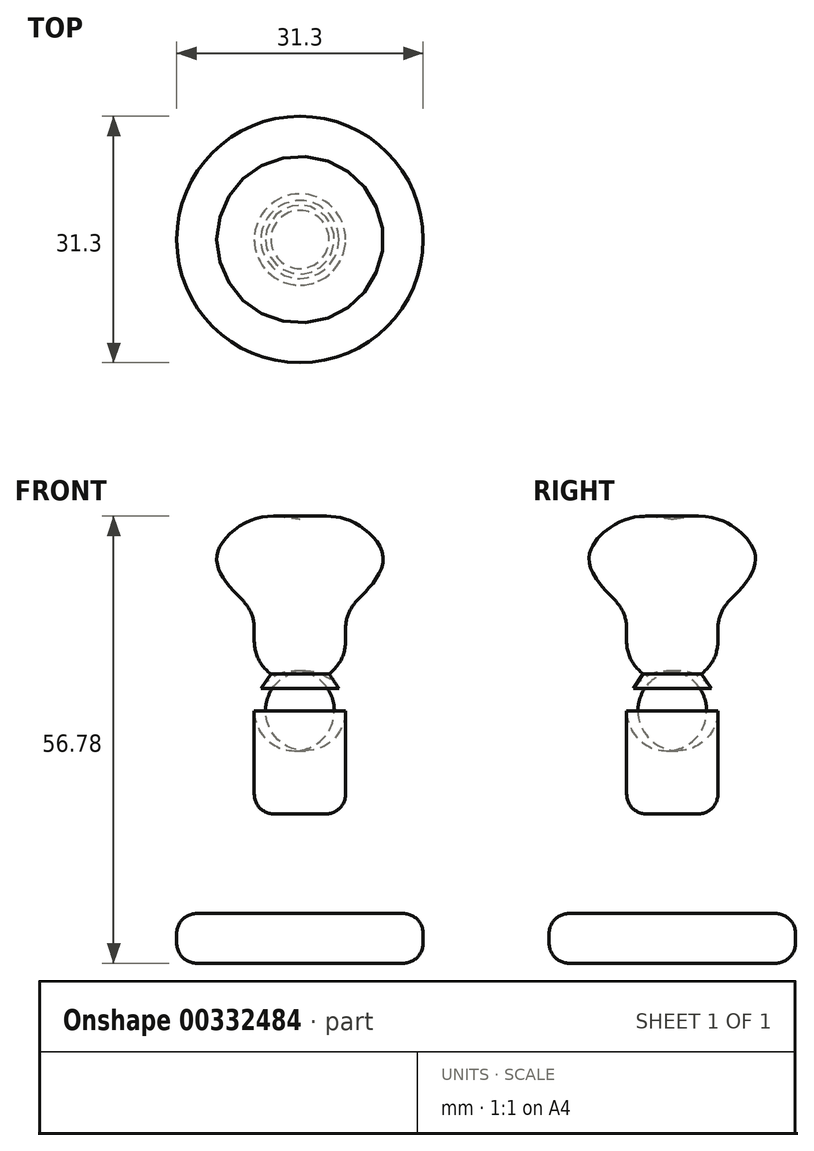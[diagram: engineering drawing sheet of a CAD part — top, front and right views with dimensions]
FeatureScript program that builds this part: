
annotation { "Feature Type Name" : "Feature", "Feature Type Description" : "" }
export const myFeature = defineFeature(function(context is Context, id is Id, definition is map)
    precondition{}
    {
        {
            var Q0;
            Q0=qCreatedBy(makeId("Front.planeOp"),FACE);
            var sketch = newSketch(context, id + "F0", { "sketchPlane" : qUnion([Q0])});
            skLineSegment(sketch, "E0.bottom", {"start": v(0, -56.42) * mm, "end": v(-15.65, -56.42) * mm});
            skLineSegment(sketch, "E0.top", {"start": v(0, -50.1) * mm, "end": v(-15.65, -50.1) * mm});
            skLineSegment(sketch, "E0.left", {"start": v(0, -56.42) * mm, "end": v(0, -50.1) * mm});
            skLineSegment(sketch, "E0.right", {"start": v(-15.65, -56.42) * mm, "end": v(-15.65, -50.1) * mm});
            skLineSegment(sketch, "E1.bottom", {"start": v(0, -50.1) * mm, "end": v(-14.3, -50.1) * mm});
            skLineSegment(sketch, "E1.top", {"start": v(0, -44.24) * mm, "end": v(-14.3, -44.24) * mm});
            skLineSegment(sketch, "E1.left", {"start": v(0, -50.1) * mm, "end": v(0, -44.24) * mm});
            skLineSegment(sketch, "E1.right", {"start": v(-14.3, -50.1) * mm, "end": v(-14.3, -44.24) * mm});
            skLineSegment(sketch, "E2.bottom", {"start": v(0, -44.24) * mm, "end": v(-11.6, -44.24) * mm});
            skLineSegment(sketch, "E2.top", {"start": v(0, -37.47) * mm, "end": v(-11.6, -37.47) * mm});
            skLineSegment(sketch, "E2.left", {"start": v(0, -44.24) * mm, "end": v(0, -37.47) * mm});
            skLineSegment(sketch, "E2.right", {"start": v(-11.6, -44.24) * mm, "end": v(-11.6, -37.47) * mm});
            skLineSegment(sketch, "E3", {"start": v(-5.8, -37.47) * mm, "end": v(-5.8, -22.81) * mm});
            skLineSegment(sketch, "E4", {"start": v(-5.8, -22.81) * mm, "end": v(-3.7, -19.65) * mm});
            skLineSegment(sketch, "E5", {"start": v(-3.7, -19.65) * mm, "end": v(-5.8, -18.26) * mm});
            skLineSegment(sketch, "E6", {"start": v(-5.8, -18.26) * mm, "end": v(-5.8, -11.76) * mm});
            skFitSpline(sketch, "E7", {"points": [v(-5.8, -11.76) * mm, v(-10.01, -7.02) * mm, v(-10.24, -3.64) * mm, v(-5.8, 0) * mm, v(0, 0) * mm], "startDerivative": vector(-18.47, 17.4) * mm, "endDerivative": vector(22.22, -3.54) * mm});
            skFitSpline(sketch, "E8", {"points": [v(-5.8, -11.76) * mm, v(0, -11.76) * mm], "startDerivative": vector(5.8, 0) * mm, "endDerivative": vector(5.8, 0) * mm});
            skLineSegment(sketch, "E9", {"start": v(0, 0) * mm, "end": v(0, -56.42) * mm});
            skSolve(sketch);
        }
        {
            var Q0;
            {var subQ1=sQuery(id+"F0.wireOp",EDGE,"E0.bottom");Q0=makeQuery(id+"F0.imprint","IMPRINT",FACE,{"disambiguationData":[TD([[makeQuery(id+"F0.imprint","IMPRINT",EDGE,{"derivedFrom":subQ1}),-1.0]])]});}
            var Q1;
            {var subQ1=sQuery(id+"F0.wireOp",EDGE,"E1.bottom");Q1=makeQuery(id+"F0.imprint","IMPRINT",FACE,{"disambiguationData":[TD([[makeQuery(id+"F0.imprint","IMPRINT",EDGE,{"derivedFrom":subQ1}),-1.0]])]});}
            var Q2;
            {var subQ5=sQuery(id+"F0.wireOp",EDGE,"E2.bottom");Q2=makeQuery(id+"F0.imprint","IMPRINT",FACE,{"disambiguationData":[TD([[makeQuery(id+"F0.imprint","IMPRINT",EDGE,{"derivedFrom":subQ5}),-1.0]])]});}
            var Q3;
            {var subQ0=sQuery(id+"F0.wireOp",EDGE,"E3");Q3=makeQuery(id+"F0.imprint","IMPRINT",FACE,{"disambiguationData":[TD([[makeQuery(id+"F0.imprint","IMPRINT",EDGE,{"derivedFrom":subQ0}),-1.0]])]});}
            var Q4;
            {var subQ0=sQuery(id+"F0.wireOp",EDGE,"E7");Q4=makeQuery(id+"F0.imprint","IMPRINT",FACE,{"disambiguationData":[TD([[makeQuery(id+"F0.imprint","IMPRINT",EDGE,{"derivedFrom":subQ0}),-1.0]])]});}
            var Q5;
            Q5=sQuery(id+"F0.wireOp",EDGE,"E9");
            revolve(context, id + "F1", {"entities" : qUnion([Q0, Q1, Q2, Q3, Q4]), "axis" : qUnion([Q5]), "revolveType" : RevolveType.FULL});
        }
        {
            var Q0;
            Q0=makeQuery(id+"F1.opRevolve","SWEPT_EDGE",EDGE,{"disambiguationData":[OSD([sQuery(id+"F0.wireOp",EDGE,"E2.top"),sQuery(id+"F0.wireOp",EDGE,"E2.right")])]});
            var Q1;
            Q1=makeQuery(id+"F1.opRevolve","SWEPT_FACE",FACE,{"disambiguationData":[OSD([sQuery(id+"F0.wireOp",EDGE,"E0.right")])]});
            var Q2;
            Q2=makeQuery(id+"F1.opRevolve","SWEPT_EDGE",EDGE,{"disambiguationData":[OSD([sQuery(id+"F0.wireOp",EDGE,"E1.top"),sQuery(id+"F0.wireOp",EDGE,"E1.right")])]});
            fillet(context, id + "F2", {"entities" : qUnion([Q0, Q1, Q2]), "radius" : 2.54 * mm, "tangentPropagation" : true, "allowEdgeOverflow" : false});
        }
        {
            var Q0;
            Q0=makeQuery(id+"F1.opRevolve","SWEPT_FACE",FACE,{"disambiguationData":[OSD([sQuery(id+"F0.wireOp",EDGE,"E6")])]});
            var Q1;
            Q1=makeQuery(id+"F1.opRevolve","SWEPT_FACE",FACE,{"disambiguationData":[OSD([sQuery(id+"F0.wireOp",EDGE,"E3")])]});
            fillet(context, id + "F3", {"entities" : qUnion([Q0, Q1]), "radius" : 5.08 * mm, "tangentPropagation" : true, "allowEdgeOverflow" : false});
        }
    });
